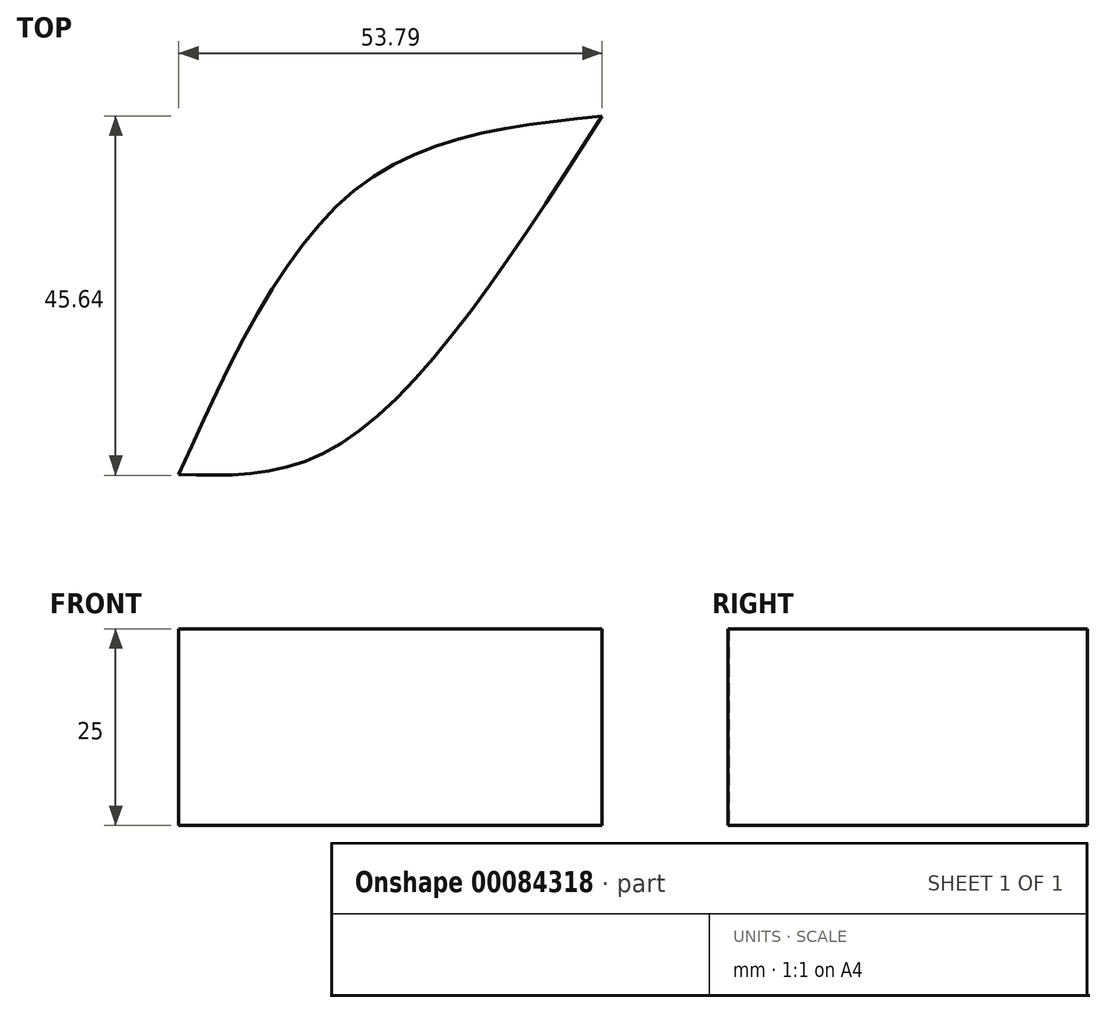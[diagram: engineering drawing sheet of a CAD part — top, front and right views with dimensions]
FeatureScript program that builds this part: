
annotation { "Feature Type Name" : "Feature", "Feature Type Description" : "" }
export const myFeature = defineFeature(function(context is Context, id is Id, definition is map)
    precondition{}
    {
        {
            var Q0;
            Q0=qCreatedBy(makeId("Top.planeOp"),FACE);
            var sketch = newSketch(context, id + "F0", { "sketchPlane" : qUnion([Q0])});
            skFitSpline(sketch, "E0", {"points": [v(0, 0) * mm, v(20.11, 3.63) * mm, v(53.8, 45.55) * mm], "startDerivative": vector(52.4, -1.57) * mm, "endDerivative": vector(54.97, 85.77) * mm});
            skFitSpline(sketch, "E1", {"points": [v(0, 0) * mm, v(23.26, 36.83) * mm, v(53.8, 45.55) * mm], "startDerivative": vector(36.87, 81.58) * mm, "endDerivative": vector(71.63, 7.58) * mm});
            skSolve(sketch);
        }
        {
            var Q0;
            Q0 = qSketchRegion(id + "F0", true);
            extrude(context, id + "F1", {"entities" : qUnion([Q0]), "depth" : 25 * mm});
        }
    });
